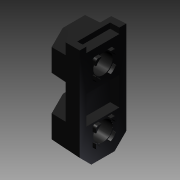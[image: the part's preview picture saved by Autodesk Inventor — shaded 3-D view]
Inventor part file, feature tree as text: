
AUTODESK INVENTOR PART (.ipt)
format: ipt  version: 2012 (Build 160160000, 160)  size: 233,472 bytes
history: native  units: in
note: dims shown in document units (in); Inventor stores cm internally (conversion verified against a paired STEP export)
features: other x1, imported_body x1, plane x1, split x1
ambient origin geometry x8: Origin, YZ Plane, XZ Plane, XY Plane, X Axis, Y Axis, Z Axis, Center Point
feature tree (4):
  parser-record x1  (decoder bookkeeping rows leaked as tree rows — omitted from the tree; the rows remain in map.json)
  imported_body  "Base1"
  plane  "Work Plane2"
  split  "Split1"
